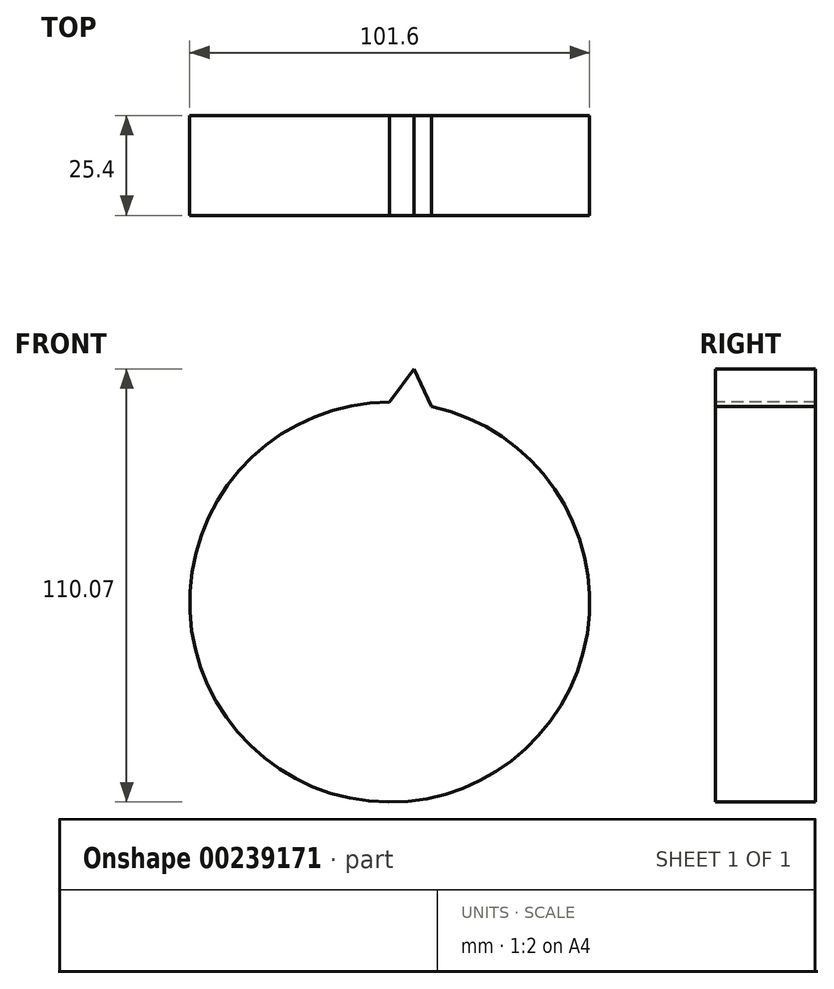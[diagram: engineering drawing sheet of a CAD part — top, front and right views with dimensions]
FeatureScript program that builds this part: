
annotation { "Feature Type Name" : "Feature", "Feature Type Description" : "" }
export const myFeature = defineFeature(function(context is Context, id is Id, definition is map)
    precondition{}
    {
        {
            var Q0;
            Q0=qCreatedBy(makeId("Front.planeOp"),FACE);
            var sketch = newSketch(context, id + "F0", { "sketchPlane" : qUnion([Q0])});
            skCircle(sketch, "E0", {"center": v(0, 0) * mm, "radius": 50.8 * mm});
            skSolve(sketch);
        }
        {
            var Q0;
            Q0 = qSketchRegion(id + "F0", true);
            extrude(context, id + "F1", {"entities" : qUnion([Q0]), "endBound" : BoundingType.SYMMETRIC, "depth" : 25.4 * mm});
        }
        {
            var Q0;
            Q0=makeQuery(id+"F1.opExtrude","CAP_FACE",FACE,{"disambiguationData":[OSD([sQuery(id+"F0.wireOp",EDGE,"E0")])],"isStart":false});
            var sketch = newSketch(context, id + "F2", { "sketchPlane" : qUnion([Q0])});
            skLineSegment(sketch, "E1", {"start": v(10.56, 49.69) * mm, "end": v(6.16, 59.27) * mm});
            skLineSegment(sketch, "E2", {"start": v(6.16, 59.27) * mm, "end": v(0, 50.8) * mm});
            skLineSegment(sketch, "E3", {"start": v(0, 50.8) * mm, "end": v(0, 0) * mm, "construction": true});
            skLineSegment(sketch, "E4", {"start": v(0, 0) * mm, "end": v(10.56, 49.69) * mm, "construction": true});
            skArc(sketch, "E5.0", {"start": v(10.56, 49.69) * mm, "mid": v(5.31, 50.52) * mm, "end": v(0, 50.8) * mm});
            skSolve(sketch);
        }
        {
            var Q0;
            Q0 = qSketchRegion(id + "F2", true);
            extrude(context, id + "F3", {"entities" : qUnion([Q0]), "operationType" : NewBodyOperationType.ADD, "oppositeDirection" : true, "depth" : 25.4 * mm});
        }
    });
